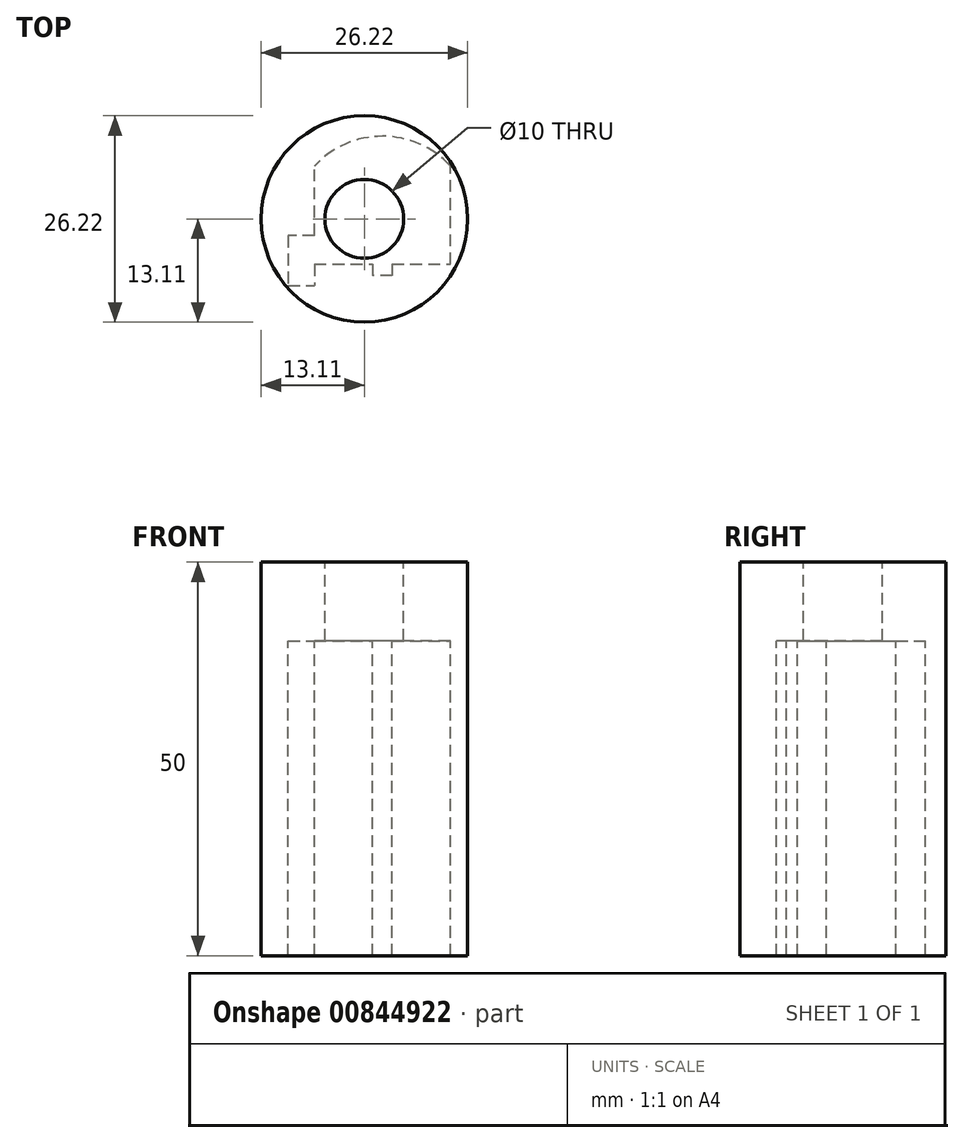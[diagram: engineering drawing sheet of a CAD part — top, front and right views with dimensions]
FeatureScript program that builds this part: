
annotation { "Feature Type Name" : "Feature", "Feature Type Description" : "" }
export const myFeature = defineFeature(function(context is Context, id is Id, definition is map)
    precondition{}
    {
        {
            var Q0;
            Q0=qCreatedBy(makeId("Top.planeOp"),FACE);
            var sketch = newSketch(context, id + "F0", { "sketchPlane" : qUnion([Q0])});
            skCircle(sketch, "E0", {"center": v(0, 0) * mm, "radius": 13.12 * mm, "construction": true});
            skSolve(sketch);
        }
        {
            var Q0;
            Q0=qCreatedBy(makeId("Top.planeOp"),FACE);
            var sketch = newSketch(context, id + "F1", { "sketchPlane" : qUnion([Q0])});
            skCircle(sketch, "E1", {"center": v(0, 0) * mm, "radius": 13.1 * mm});
            skCircle(sketch, "E2", {"center": v(0, 0) * mm, "radius": 5 * mm});
            skCircle(sketch, "E3.0", {"center": v(0, 0) * mm, "radius": 13.12 * mm});
            skSolve(sketch);
        }
        {
            var Q0;
            Q0=makeQuery(id+"F1.imprint","IMPRINT",FACE,{"disambiguationData":[TD([[makeQuery(id+"F1.imprint","IMPRINT",EDGE,{"derivedFrom":sQuery(id+"F1.wireOp",EDGE,"E1")}),1.0]])]});
            extrude(context, id + "F2", {"entities" : qUnion([Q0]), "oppositeDirection" : true, "depth" : 25 * mm, "offsetDistance" : 25 * mm, "hasSecondDirection" : true, "secondDirectionOppositeDirection" : false, "secondDirectionDepth" : 25 * mm});
        }
        {
            var Q0;
            Q0=qCreatedBy(makeId("Top.planeOp"),FACE);
            cPlane(context, id + "F3", {"entities" : qUnion([Q0]), "cplaneType" : CPlaneType.OFFSET, "offset" : 15 * mm, "width" : 150 * mm, "height" : 150 * mm});
        }
        {
            var Q0;
            Q0=qCreatedBy(id+"F3.planeOp",FACE);
            var sketch = newSketch(context, id + "F4", { "sketchPlane" : qUnion([Q0])});
            skLineSegment(sketch, "E4.bottom", {"start": v(-9.69, -3.55) * mm, "end": v(10.91, -3.55) * mm});
            skLineSegment(sketch, "E4.top", {"start": v(-9.69, -5.76) * mm, "end": v(10.91, -5.76) * mm});
            skLineSegment(sketch, "E4.left", {"start": v(-9.69, -3.55) * mm, "end": v(-9.69, -5.76) * mm});
            skLineSegment(sketch, "E4.right", {"start": v(10.91, -3.55) * mm, "end": v(10.91, -5.76) * mm});
            skLineSegment(sketch, "E5.0", {"start": v(-6.34, -5.76) * mm, "end": v(1.01, -5.76) * mm});
            skLineSegment(sketch, "E6.top", {"start": v(3.52, -7.17) * mm, "end": v(1.01, -7.17) * mm});
            skLineSegment(sketch, "E6.left", {"start": v(3.52, -5.76) * mm, "end": v(3.52, -7.17) * mm});
            skLineSegment(sketch, "E6.right", {"start": v(1.01, -5.76) * mm, "end": v(1.01, -7.17) * mm});
            skLineSegment(sketch, "E7.top", {"start": v(-9.69, -8.47) * mm, "end": v(-6.34, -8.47) * mm});
            skLineSegment(sketch, "E7.left", {"start": v(-9.69, -5.76) * mm, "end": v(-9.69, -8.47) * mm});
            skLineSegment(sketch, "E7.right", {"start": v(-6.34, -5.76) * mm, "end": v(-6.34, -8.47) * mm});
            skLineSegment(sketch, "E8.trimOffspring", {"start": v(3.52, -5.76) * mm, "end": v(10.91, -5.76) * mm});
            skLineSegment(sketch, "E9.bottom", {"start": v(-6.34, -3.55) * mm, "end": v(-9.69, -3.55) * mm});
            skLineSegment(sketch, "E9.top", {"start": v(-6.34, -2.11) * mm, "end": v(-9.69, -2.11) * mm});
            skLineSegment(sketch, "E9.left", {"start": v(-6.34, -3.55) * mm, "end": v(-6.34, -2.11) * mm});
            skLineSegment(sketch, "E9.right", {"start": v(-9.69, -3.55) * mm, "end": v(-9.69, -2.11) * mm});
            skLineSegment(sketch, "E10.bottom", {"start": v(10.91, -3.55) * mm, "end": v(-6.34, -3.55) * mm});
            skLineSegment(sketch, "E10.top", {"start": v(10.91, 6.73) * mm, "end": v(-6.34, 6.73) * mm});
            skLineSegment(sketch, "E10.left", {"start": v(10.91, -3.55) * mm, "end": v(10.91, 6.73) * mm});
            skLineSegment(sketch, "E10.right", {"start": v(-6.34, -3.55) * mm, "end": v(-6.34, 6.73) * mm});
            skArc(sketch, "E11", {"start": v(10.91, 6.73) * mm, "mid": v(2.29, 10.5) * mm, "end": v(-6.34, 6.73) * mm});
            skSolve(sketch);
        }
        {
            var Q0;
            {var subQ8=sQuery(id+"F4.wireOp",EDGE,"E9.left");var subQ12=sQuery(id+"F4.wireOp",EDGE,"E4.left");var subQ19=makeQuery(id+"F4.imprint","IMPRINT",EDGE,{"derivedFrom":sQuery(id+"F4.wireOp",EDGE,"E10.top")});var subQ20=makeQuery(id+"F4.imprint","IMPRINT",EDGE,{"derivedFrom":subQ8});Q0=qUnion([makeQuery(id+"F4.imprint","IMPRINT",FACE,{"disambiguationData":[TD([[makeQuery(id+"F4.imprint","IMPRINT",EDGE,{"derivedFrom":sQuery(id+"F4.wireOp",EDGE,"E7.top")}),1.0]])]}),makeQuery(id+"F4.imprint","IMPRINT",FACE,{"disambiguationData":[TD([[makeQuery(id+"F4.imprint","IMPRINT",EDGE,{"derivedFrom":sQuery(id+"F4.wireOp",EDGE,"E6.top")}),-1.0]])]}),makeQuery(id+"F4.imprint","IMPRINT",FACE,{"disambiguationData":[TD([[subQ19,-1.0]])]}),makeQuery(id+"F4.imprint","IMPRINT",FACE,{"disambiguationData":[TD([[makeQuery(id+"F4.imprint","IMPRINT",EDGE,{"derivedFrom":sQuery(id+"F4.wireOp",EDGE,"E9.top")}),1.0]])]}),makeQuery(id+"F4.imprint","IMPRINT",FACE,{"disambiguationData":[TD([[subQ20,-1.0]])]}),makeQuery(id+"F4.imprint","IMPRINT",FACE,{"disambiguationData":[TD([[makeQuery(id+"F4.imprint","IMPRINT",EDGE,{"derivedFrom":subQ12}),1.0]])]})]);}
            extrude(context, id + "F5", {"entities" : qUnion([Q0]), "operationType" : NewBodyOperationType.REMOVE, "oppositeDirection" : true, "depth" : 43 * mm, "offsetDistance" : 25 * mm});
        }
    });
